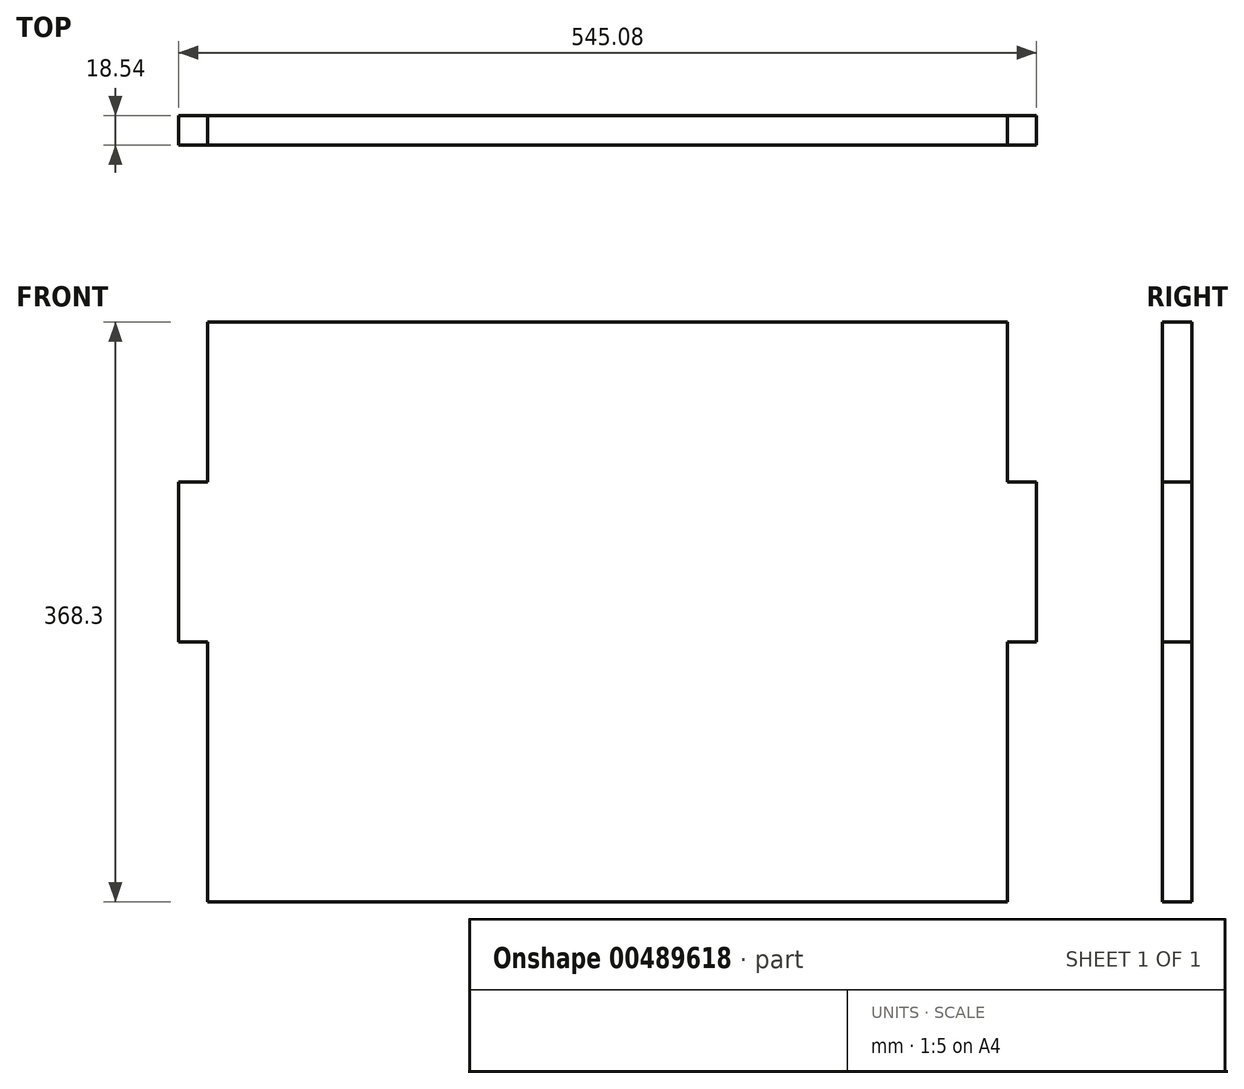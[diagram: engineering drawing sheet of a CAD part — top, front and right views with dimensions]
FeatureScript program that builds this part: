
annotation { "Feature Type Name" : "Feature", "Feature Type Description" : "" }
export const myFeature = defineFeature(function(context is Context, id is Id, definition is map)
    precondition{}
    {
        {
            var Q0;
            Q0=qCreatedBy(makeId("Front.planeOp"),FACE);
            var sketch = newSketch(context, id + "F0", { "sketchPlane" : qUnion([Q0])});
            skLineSegment(sketch, "E0.top", {"start": v(-254, 152.4) * mm, "end": v(254, 152.4) * mm});
            skPoint(sketch, "E0.middle", {"position": v(0, 0) * mm});
            skLineSegment(sketch, "E1", {"start": v(-254, -50.8) * mm, "end": v(-272.54, -50.8) * mm});
            skLineSegment(sketch, "E2", {"start": v(-272.54, -50.8) * mm, "end": v(-272.54, 50.8) * mm});
            skLineSegment(sketch, "E3", {"start": v(-272.54, 50.8) * mm, "end": v(-254, 50.8) * mm});
            skLineSegment(sketch, "E4", {"start": v(254, -50.8) * mm, "end": v(272.54, -50.8) * mm});
            skLineSegment(sketch, "E5", {"start": v(272.54, -50.8) * mm, "end": v(272.54, 50.8) * mm});
            skLineSegment(sketch, "E6", {"start": v(272.54, 50.8) * mm, "end": v(254, 50.8) * mm});
            skLineSegment(sketch, "E7.trimOffspring", {"start": v(254, 50.8) * mm, "end": v(254, 152.4) * mm});
            skLineSegment(sketch, "E8.trimOffspring", {"start": v(-254, 50.8) * mm, "end": v(-254, 152.4) * mm});
            skLineSegment(sketch, "E9", {"start": v(-254, -50.8) * mm, "end": v(-254, -215.9) * mm});
            skLineSegment(sketch, "E10", {"start": v(-254, -215.9) * mm, "end": v(254, -215.9) * mm});
            skLineSegment(sketch, "E11", {"start": v(254, -50.8) * mm, "end": v(254, -215.9) * mm});
            skSolve(sketch);
        }
        {
            var Q0;
            Q0=makeQuery(id+"F0.imprint","IMPRINT",FACE,{"disambiguationData":[TD([[makeQuery(id+"F0.imprint","IMPRINT",EDGE,{"derivedFrom":sQuery(id+"F0.wireOp",EDGE,"E0.top")}),-1.0]])]});
            extrude(context, id + "F1", {"entities" : qUnion([Q0]), "depth" : 18.54 * mm, "offsetDistance" : 25.4 * mm});
        }
    });
